# Revit family: Shinhoo_MEGA_F
name_source: partatom
category: Оборудование
units: mm (PartAtom-declared; Revit-internal decimal feet)

## family parameters
Всегда вертикально = Нет
Классификация = Нет
На основе рабочей плоскости = Нет
Общий = Нет
При загрузке вырезать с полостями = Нет
Размер круглого соединителя = Использовать диаметр
Тип детали = Вставляется
Точка расчета площади = Нет

## types (2) — shared parameters
ADSK_URL страницы изделия = https://shinhoopump.ru
ADSK_Версия Revit = 2019
ADSK_Версия семейства = 1.0
ADSK_Единица измерения = шт
ADSK_Завод-изготовитель = Shinhoo
ADSK_Количество = 1
ADSK_Коэффициент мощности = 1
ADSK_Масса = 7.6
ADSK_Масса_Текст = 7.6
ADSK_Материал = Чугун с катафорезным покрытием
ADSK_Напряжение = 230 В
ADSK_Обозначение = ГОСТ 31839-2012, ГОСТ 12.2.007.0-75, ГОСТ 12.2.003-91, ГОСТ Р МЭК 60204-1-2007,  ГОСТ 30804
ADSK_Ток = 1 А
B = 160 мм
B1 = 80 мм
B2 = 80 мм
DN = 40 мм
H = 206 мм
H1 = 62 мм
H2 = 144 мм
L = 220 мм
URL = https://shinhoopump.ru
b1_20 = 69 мм
d1 = 50 мм
d6 = 100 мм
r1 = 25 мм
r1_1 = 26 мм
r1_3 = 38 мм
r6 = 55 мм
Изготовитель = Shinhoo
Класс защиты (IP) = IP42
Разработчик = ООО ПРОРУБИМ
Разработчик (телефон) = +7(495)649-85-43
Скорость вращения = 2850
Степень защиты от удара (IK) = IK04
Тип Насоса = Регулируемый высокоэффективный циркуляционный насос с «мокрым» ротором
Тип основания = встроенный

## per-type parameters (varying)
| type | ADSK_Код изделия | ADSK_Наименование | ADSK_Наименование краткое | ADSK_Номинальная мощность | ADSK_Полная мощность | ADSK_Расход жидкости | Группа модели |
| MEGA 40-6F 220 1x230В - 71121005 | 71121005 | Регулируемый высокоэффективный циркуляционный насос с «мокрым» ротором MEGA 40-6F 220 1x230В | MEGA 40-6F 220 1x230В | 90 Вт | 90 В·А | 0.001667 м³/с | MEGA 40-6F 220 1x230В |
| MEGA 40-10F 220 1x230В - 71121006 | 71121006 | Регулируемый высокоэффективный циркуляционный насос с «мокрым» ротором MEGA 40-10F 220 1x230В | MEGA 40-10F 220 1x230В | 185 Вт | 185 В·А | 0.003056 м³/с | MEGA 40-10F 220 1x230В |

## geometry (parser evidence)
native form markers: Sweep x2
no freeform markers — native parametric forms only
